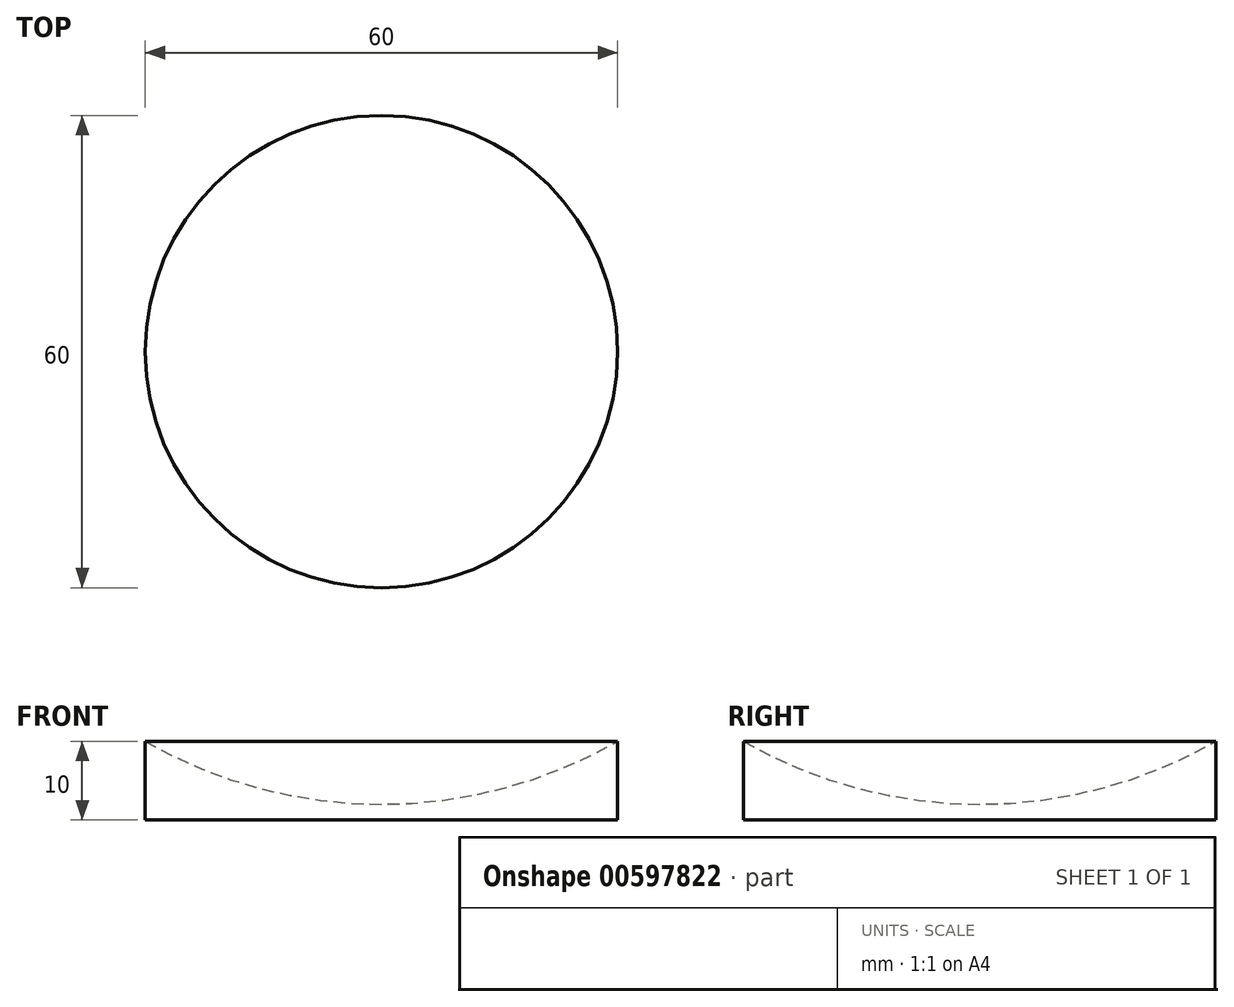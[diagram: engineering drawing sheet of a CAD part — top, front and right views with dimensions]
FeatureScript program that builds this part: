
annotation { "Feature Type Name" : "Feature", "Feature Type Description" : "" }
export const myFeature = defineFeature(function(context is Context, id is Id, definition is map)
    precondition{}
    {
        {
            var Q0;
            Q0=qCreatedBy(makeId("Front.planeOp"),FACE);
            var sketch = newSketch(context, id + "F0", { "sketchPlane" : qUnion([Q0])});
            skCircle(sketch, "E0", {"center": v(0, 0) * mm, "radius": 60.25 * mm});
            skLineSegment(sketch, "E1", {"start": v(-30, -52.25) * mm, "end": v(30, -52.25) * mm});
            skPoint(sketch, "E2", {"position": v(0, -52.25) * mm});
            skPoint(sketch, "E3", {"position": v(0, -60.25) * mm});
            skLineSegment(sketch, "E4.top", {"start": v(-30, -62.25) * mm, "end": v(30, -62.25) * mm});
            skLineSegment(sketch, "E4.left", {"start": v(-30, -52.25) * mm, "end": v(-30, -62.25) * mm});
            skLineSegment(sketch, "E4.right", {"start": v(30, -52.25) * mm, "end": v(30, -62.25) * mm});
            skSolve(sketch);
        }
        {
            var Q0;
            Q0=makeQuery(id+"F0.imprint","IMPRINT",FACE,{"disambiguationData":[TD([[makeQuery(id+"F0.imprint","IMPRINT",EDGE,{"derivedFrom":sQuery(id+"F0.wireOp",EDGE,"E4.top")}),1.0]])]});
            var Q1;
            {var subQ0=sQuery(id+"F0.wireOp",EDGE,"E1");Q1=makeQuery(id+"F0.imprint","IMPRINT",FACE,{"disambiguationData":[TD([[makeQuery(id+"F0.imprint","IMPRINT",EDGE,{"derivedFrom":subQ0}),-1.0]])]});}
            extrude(context, id + "F1", {"entities" : qUnion([Q0, Q1]), "depth" : 30 * mm, "offsetDistance" : 25 * mm, "hasSecondDirection" : true, "secondDirectionOppositeDirection" : true, "secondDirectionDepth" : 30 * mm});
        }
        {
            var Q0;
            Q0=qCreatedBy(makeId("Front.planeOp"),FACE);
            var sketch = newSketch(context, id + "F2", { "sketchPlane" : qUnion([Q0])});
            skCircle(sketch, "E5", {"center": v(0, 0) * mm, "radius": 60.25 * mm});
            skLineSegment(sketch, "E6", {"start": v(-30, -52.25) * mm, "end": v(30, -52.25) * mm});
            skPoint(sketch, "E7", {"position": v(0, -52.25) * mm});
            skPoint(sketch, "E8", {"position": v(0, -60.25) * mm});
            skLineSegment(sketch, "E9.top", {"start": v(-30, -62.25) * mm, "end": v(30, -62.25) * mm});
            skLineSegment(sketch, "E9.left", {"start": v(-30, -52.25) * mm, "end": v(-30, -62.25) * mm});
            skLineSegment(sketch, "E9.right", {"start": v(30, -52.25) * mm, "end": v(30, -62.25) * mm});
            skSolve(sketch);
        }
        {
            var Q0;
            Q0=qCreatedBy(makeId("Top.planeOp"),FACE);
            var sketch = newSketch(context, id + "F3", { "sketchPlane" : qUnion([Q0])});
            skCircle(sketch, "E10", {"center": v(0, 0) * mm, "radius": 60.25 * mm});
            skSolve(sketch);
        }
        {
            var Q0;
            Q0=qSketchRegion(id+"F3",true);
            var Q1;
            Q1=sQuery(id+"F2.wireOp",EDGE,"E5");
            sweep(context, id + "F4", {"operationType" : NewBodyOperationType.REMOVE, "profiles" : qUnion([Q0]), "path" : qUnion([Q1])});
        }
        {
            var Q0;
            Q0=makeQuery(id+"F1.opExtrude","CAP_EDGE",EDGE,{"disambiguationData":[OSD([sQuery(id+"F0.wireOp",EDGE,"E4.left")])],"isStart":false});
            var Q1;
            Q1=makeQuery(id+"F1.opExtrude","CAP_EDGE",EDGE,{"disambiguationData":[OSD([sQuery(id+"F0.wireOp",EDGE,"E4.right")])],"isStart":false});
            var Q2;
            Q2=makeQuery(id+"F1.opExtrude","CAP_EDGE",EDGE,{"disambiguationData":[OSD([sQuery(id+"F0.wireOp",EDGE,"E4.right")])],"isStart":true});
            var Q3;
            Q3=makeQuery(id+"F1.opExtrude","CAP_EDGE",EDGE,{"disambiguationData":[OSD([sQuery(id+"F0.wireOp",EDGE,"E4.left")])],"isStart":true});
            fillet(context, id + "F5", {"entities" : qUnion([Q0, Q1, Q2, Q3]), "radius" : 30 * mm, "tangentPropagation" : true, "allowEdgeOverflow" : false});
        }
    });
